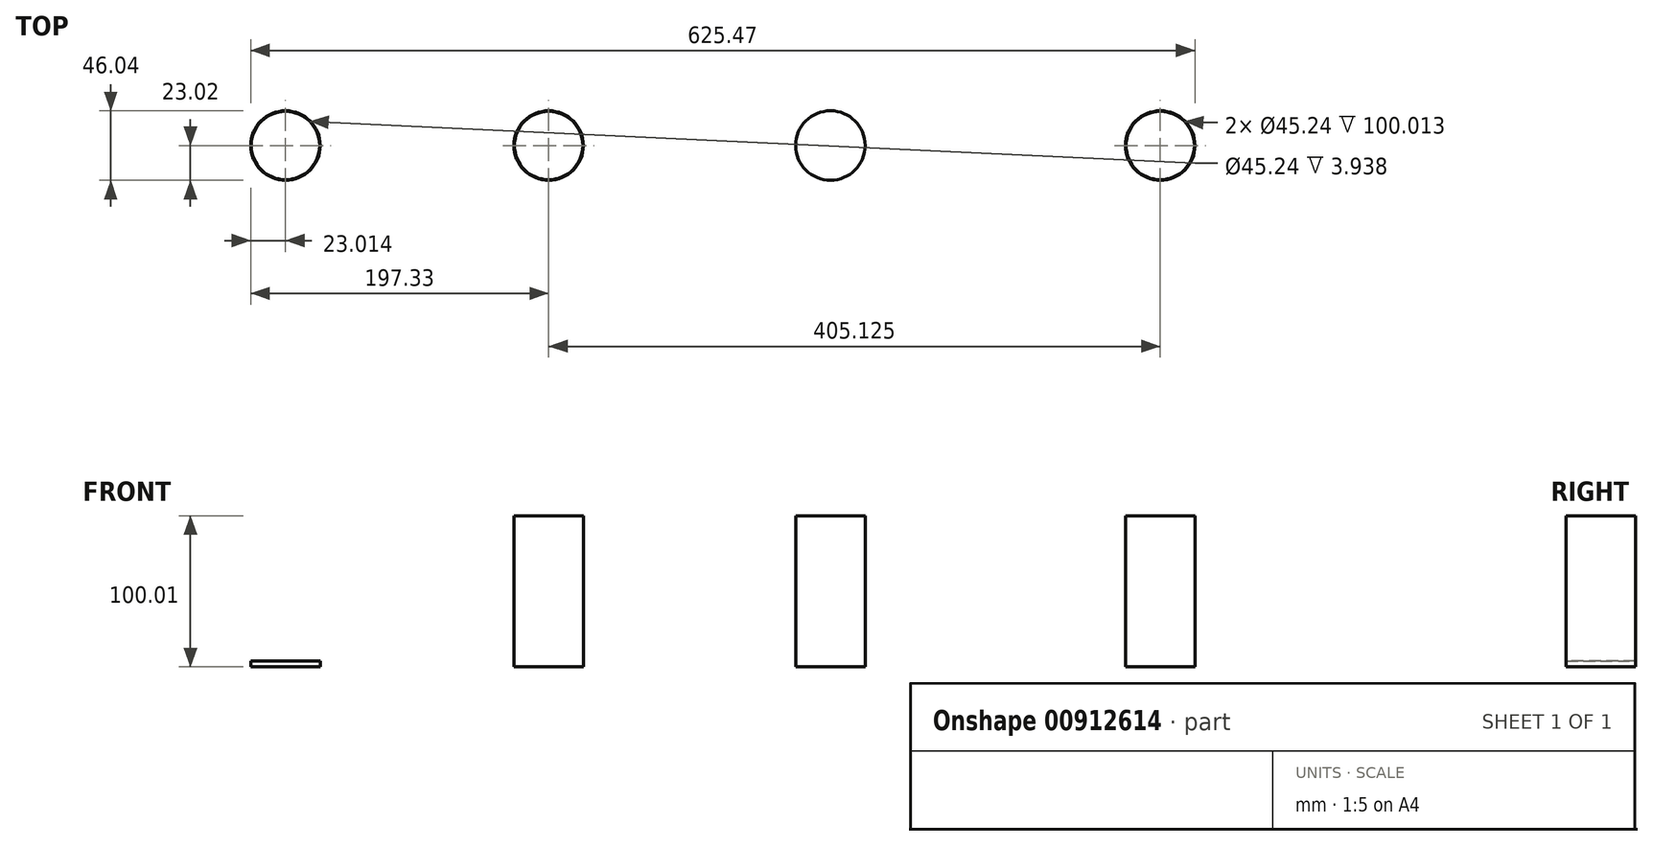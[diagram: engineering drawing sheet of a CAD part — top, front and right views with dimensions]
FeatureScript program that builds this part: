
annotation { "Feature Type Name" : "Feature", "Feature Type Description" : "" }
export const myFeature = defineFeature(function(context is Context, id is Id, definition is map)
    precondition{}
    {
        {
            var Q0;
            Q0=qCreatedBy(makeId("Top.planeOp"),FACE);
            var sketch = newSketch(context, id + "F0", { "sketchPlane" : qUnion([Q0])});
            skCircle(sketch, "E0", {"center": v(79.97, 0) * mm, "radius": 23.02 * mm});
            skCircle(sketch, "E1.0", {"center": v(79.97, 0) * mm, "radius": 22.62 * mm});
            skSolve(sketch);
        }
        {
            var Q0;
            Q0 = qSketchRegion(id + "F0", true);
            extrude(context, id + "F1", {"entities" : qUnion([Q0]), "depth" : (3 + (15 / 16)) * mm, "offsetDistance" : 25.4 * mm});
        }
        {
            var Q0;
            Q0=qCreatedBy(makeId("Front.planeOp"),FACE);
            var sketch = newSketch(context, id + "F2", { "sketchPlane" : qUnion([Q0])});
            skLineSegment(sketch, "E2.bottom", {"start": v(276.91, 0) * mm, "end": v(277.3, 0) * mm});
            skLineSegment(sketch, "E2.top", {"start": v(276.91, 100.01) * mm, "end": v(277.3, 100.01) * mm});
            skLineSegment(sketch, "E2.left", {"start": v(276.91, 0) * mm, "end": v(276.91, 100.01) * mm});
            skLineSegment(sketch, "E2.right", {"start": v(277.3, 0) * mm, "end": v(277.3, 100.01) * mm});
            skLineSegment(sketch, "E3", {"start": v(254.3, 0) * mm, "end": v(254.3, 135.6) * mm, "construction": true});
            skLineSegment(sketch, "E4", {"start": v(277.3, 24.36) * mm, "end": v(254.3, 24.36) * mm, "construction": true});
            skSolve(sketch);
        }
        {
            var Q0;
            Q0 = qSketchRegion(id + "F2", true);
            var Q1;
            Q1=sQuery(id+"F2.wireOp",EDGE,"E3");
            revolve(context, id + "F3", {"surfaceOperationType" : NewSurfaceOperationType.NEW, "entities" : qUnion([Q0]), "axis" : qUnion([Q1]), "revolveType" : RevolveType.FULL});
        }
        {
            var Q0;
            Q0=qCreatedBy(makeId("Front.planeOp"),FACE);
            var sketch = newSketch(context, id + "F4", { "sketchPlane" : qUnion([Q0])});
            skLineSegment(sketch, "E5", {"start": v(440.93, 0) * mm, "end": v(440.93, 100.01) * mm});
            skSolve(sketch);
        }
        {
            var Q0;
            Q0=qCreatedBy(makeId("Top.planeOp"),FACE);
            var sketch = newSketch(context, id + "F5", { "sketchPlane" : qUnion([Q0])});
            skPoint(sketch, "E6.0", {"position": v(440.93, 0) * mm});
            skCircle(sketch, "E7", {"center": v(440.93, 0) * mm, "radius": 23.02 * mm});
            skCircle(sketch, "E8", {"center": v(440.93, 0) * mm, "radius": 22.82 * mm});
            skSolve(sketch);
        }
        {
            var Q0;
            Q0=makeQuery(id+"F5.imprint","IMPRINT",FACE,{"disambiguationData":[TD([[makeQuery(id+"F5.imprint","IMPRINT",EDGE,{"derivedFrom":sQuery(id+"F5.wireOp",EDGE,"E8")}),1.0]])]});
            var Q1;
            Q1=makeQuery(id+"F5.imprint","IMPRINT",FACE,{"disambiguationData":[TD([[makeQuery(id+"F5.imprint","IMPRINT",EDGE,{"derivedFrom":sQuery(id+"F5.wireOp",EDGE,"E7")}),1.0]])]});
            var Q2;
            Q2=sQuery(id+"F4.wireOp",EDGE,"E5");
            sweep(context, id + "F6", {"profiles" : qUnion([Q0, Q1]), "path" : qUnion([Q2])});
        }
        {
            var Q0;
            Q0=qCreatedBy(makeId("Top.planeOp"),FACE);
            var sketch = newSketch(context, id + "F7", { "sketchPlane" : qUnion([Q0])});
            skCircle(sketch, "E9", {"center": v(659.41, 0) * mm, "radius": 22.62 * mm});
            skCircle(sketch, "E10", {"center": v(659.41, 0) * mm, "radius": 23.02 * mm});
            skSolve(sketch);
        }
        {
            var Q0;
            Q0 = qSketchRegion(id + "F7", true);
            extrude(context, id + "F8", {"entities" : qUnion([Q0]), "depth" : 100.01 * mm, "offsetDistance" : 25.4 * mm});
        }
    });
